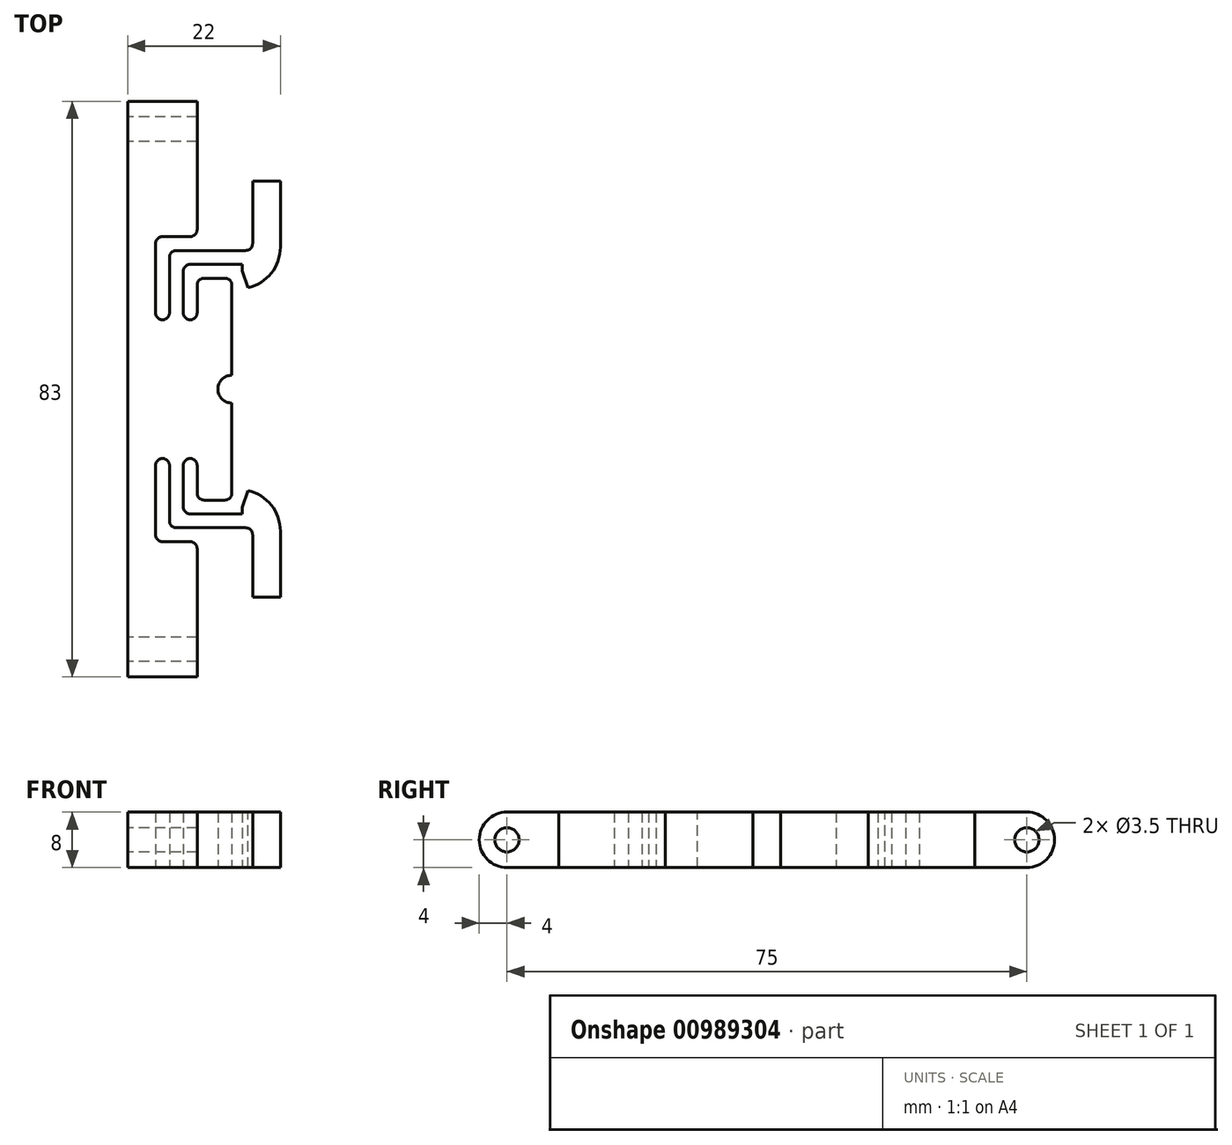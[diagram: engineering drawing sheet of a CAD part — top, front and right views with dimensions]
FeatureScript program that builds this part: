
annotation { "Feature Type Name" : "Feature", "Feature Type Description" : "" }
export const myFeature = defineFeature(function(context is Context, id is Id, definition is map)
    precondition{}
    {
        {
            var Q0;
            Q0=qCreatedBy(makeId("Top.planeOp"),FACE);
            var sketch = newSketch(context, id + "F0", { "sketchPlane" : qUnion([Q0])});
            skLineSegment(sketch, "E0.bottom", {"start": v(0, 0) * mm, "end": v(22, 0) * mm});
            skLineSegment(sketch, "E0.top", {"start": v(0, 83) * mm, "end": v(22, 83) * mm});
            skLineSegment(sketch, "E0.left", {"start": v(0, 0) * mm, "end": v(0, 83) * mm});
            skLineSegment(sketch, "E0.right", {"start": v(22, 0) * mm, "end": v(22, 83) * mm});
            skLineSegment(sketch, "E1", {"start": v(0, 41.5) * mm, "end": v(22, 41.5) * mm, "construction": true});
            skLineSegment(sketch, "E2.bottom", {"start": v(22, 59.5) * mm, "end": v(15, 59.5) * mm});
            skLineSegment(sketch, "E2.top", {"start": v(22, 23.5) * mm, "end": v(15, 23.5) * mm});
            skLineSegment(sketch, "E2.left", {"start": v(22, 59.5) * mm, "end": v(22, 23.5) * mm});
            skLineSegment(sketch, "E2.right", {"start": v(15, 59.5) * mm, "end": v(15, 23.5) * mm});
            skLineSegment(sketch, "E3", {"start": v(16.5, 59.5) * mm, "end": v(16.5, 23.5) * mm, "construction": true});
            skLineSegment(sketch, "E4.bottom", {"start": v(16.5, 59.5) * mm, "end": v(22, 59.5) * mm});
            skLineSegment(sketch, "E4.top", {"start": v(16.5, 56) * mm, "end": v(22, 56) * mm});
            skLineSegment(sketch, "E4.left", {"start": v(16.5, 59.5) * mm, "end": v(16.5, 56) * mm});
            skLineSegment(sketch, "E4.right", {"start": v(22, 59.5) * mm, "end": v(22, 56) * mm});
            skLineSegment(sketch, "E5.bottom", {"start": v(16.5, 23.5) * mm, "end": v(22, 23.5) * mm});
            skLineSegment(sketch, "E5.top", {"start": v(16.5, 27) * mm, "end": v(22, 27) * mm});
            skLineSegment(sketch, "E5.left", {"start": v(16.5, 23.5) * mm, "end": v(16.5, 27) * mm});
            skLineSegment(sketch, "E5.right", {"start": v(22, 23.5) * mm, "end": v(22, 27) * mm});
            skLineSegment(sketch, "E6", {"start": v(8, 83) * mm, "end": v(8, 0) * mm, "construction": true});
            skLineSegment(sketch, "E7.bottom", {"start": v(8, 63.5) * mm, "end": v(22, 63.5) * mm});
            skLineSegment(sketch, "E7.top", {"start": v(8, 61.5) * mm, "end": v(22, 61.5) * mm});
            skLineSegment(sketch, "E7.left", {"start": v(8, 63.5) * mm, "end": v(8, 61.5) * mm});
            skLineSegment(sketch, "E7.right", {"start": v(22, 63.5) * mm, "end": v(22, 61.5) * mm});
            skLineSegment(sketch, "E8.bottom", {"start": v(8, 21.5) * mm, "end": v(22, 21.5) * mm});
            skLineSegment(sketch, "E8.top", {"start": v(8, 19.5) * mm, "end": v(22, 19.5) * mm});
            skLineSegment(sketch, "E8.left", {"start": v(8, 21.5) * mm, "end": v(8, 19.5) * mm});
            skLineSegment(sketch, "E8.right", {"start": v(22, 21.5) * mm, "end": v(22, 19.5) * mm});
            skLineSegment(sketch, "E9.bottom", {"start": v(18, 61.5) * mm, "end": v(22, 61.5) * mm});
            skLineSegment(sketch, "E9.top", {"start": v(18, 71.5) * mm, "end": v(22, 71.5) * mm});
            skLineSegment(sketch, "E9.left", {"start": v(18, 61.5) * mm, "end": v(18, 71.5) * mm});
            skLineSegment(sketch, "E9.right", {"start": v(22, 61.5) * mm, "end": v(22, 71.5) * mm});
            skLineSegment(sketch, "E10.bottom", {"start": v(18, 21.5) * mm, "end": v(22, 21.5) * mm});
            skLineSegment(sketch, "E10.top", {"start": v(18, 11.5) * mm, "end": v(22, 11.5) * mm});
            skLineSegment(sketch, "E10.left", {"start": v(18, 21.5) * mm, "end": v(18, 11.5) * mm});
            skLineSegment(sketch, "E10.right", {"start": v(22, 21.5) * mm, "end": v(22, 11.5) * mm});
            skLineSegment(sketch, "E11.bottom", {"start": v(10, 63.5) * mm, "end": v(22, 63.5) * mm});
            skLineSegment(sketch, "E11.top", {"start": v(10, 73) * mm, "end": v(22, 73) * mm});
            skLineSegment(sketch, "E11.left", {"start": v(10, 63.5) * mm, "end": v(10, 73) * mm});
            skLineSegment(sketch, "E11.right", {"start": v(22, 63.5) * mm, "end": v(22, 73) * mm});
            skLineSegment(sketch, "E12.bottom", {"start": v(10, 19.5) * mm, "end": v(22, 19.5) * mm});
            skLineSegment(sketch, "E12.top", {"start": v(10, 10) * mm, "end": v(22, 10) * mm});
            skLineSegment(sketch, "E12.left", {"start": v(10, 19.5) * mm, "end": v(10, 10) * mm});
            skLineSegment(sketch, "E12.right", {"start": v(22, 19.5) * mm, "end": v(22, 10) * mm});
            skLineSegment(sketch, "E13.bottom", {"start": v(15, 59.5) * mm, "end": v(8, 59.5) * mm});
            skLineSegment(sketch, "E13.top", {"start": v(15, 57.5) * mm, "end": v(8, 57.5) * mm});
            skLineSegment(sketch, "E13.left", {"start": v(15, 59.5) * mm, "end": v(15, 57.5) * mm});
            skLineSegment(sketch, "E13.right", {"start": v(8, 59.5) * mm, "end": v(8, 57.5) * mm});
            skLineSegment(sketch, "E14.bottom", {"start": v(15, 23.5) * mm, "end": v(8, 23.5) * mm});
            skLineSegment(sketch, "E14.top", {"start": v(15, 25.5) * mm, "end": v(8, 25.5) * mm});
            skLineSegment(sketch, "E14.left", {"start": v(15, 23.5) * mm, "end": v(15, 25.5) * mm});
            skLineSegment(sketch, "E14.right", {"start": v(8, 23.5) * mm, "end": v(8, 25.5) * mm});
            skLineSegment(sketch, "E15.bottom", {"start": v(8, 57.5) * mm, "end": v(10, 57.5) * mm});
            skLineSegment(sketch, "E15.top", {"start": v(8, 51.5) * mm, "end": v(10, 51.5) * mm});
            skLineSegment(sketch, "E15.left", {"start": v(8, 57.5) * mm, "end": v(8, 51.5) * mm});
            skLineSegment(sketch, "E15.right", {"start": v(10, 57.5) * mm, "end": v(10, 51.5) * mm});
            skLineSegment(sketch, "E16.bottom", {"start": v(8, 25.5) * mm, "end": v(10, 25.5) * mm});
            skLineSegment(sketch, "E16.top", {"start": v(8, 31.5) * mm, "end": v(10, 31.5) * mm});
            skLineSegment(sketch, "E16.left", {"start": v(8, 25.5) * mm, "end": v(8, 31.5) * mm});
            skLineSegment(sketch, "E16.right", {"start": v(10, 25.5) * mm, "end": v(10, 31.5) * mm});
            skLineSegment(sketch, "E17.bottom", {"start": v(6, 21.5) * mm, "end": v(8, 21.5) * mm});
            skLineSegment(sketch, "E17.top", {"start": v(6, 31.5) * mm, "end": v(8, 31.5) * mm});
            skLineSegment(sketch, "E17.left", {"start": v(6, 21.5) * mm, "end": v(6, 31.5) * mm});
            skLineSegment(sketch, "E17.right", {"start": v(8, 21.5) * mm, "end": v(8, 31.5) * mm});
            skPoint(sketch, "E18.oppositeSnap0", {"position": v(6, 26.5) * mm});
            skLineSegment(sketch, "E18.bottom", {"start": v(8, 51.5) * mm, "end": v(6, 51.5) * mm});
            skLineSegment(sketch, "E18.top", {"start": v(8, 61.5) * mm, "end": v(6, 61.5) * mm});
            skLineSegment(sketch, "E18.left", {"start": v(8, 51.5) * mm, "end": v(8, 61.5) * mm});
            skLineSegment(sketch, "E18.right", {"start": v(6, 51.5) * mm, "end": v(6, 61.5) * mm});
            skLineSegment(sketch, "E19.bottom", {"start": v(8, 19.5) * mm, "end": v(4, 19.5) * mm});
            skLineSegment(sketch, "E19.top", {"start": v(8, 31.5) * mm, "end": v(4, 31.5) * mm});
            skLineSegment(sketch, "E19.left", {"start": v(8, 19.5) * mm, "end": v(8, 31.5) * mm});
            skLineSegment(sketch, "E19.right", {"start": v(4, 19.5) * mm, "end": v(4, 31.5) * mm});
            skLineSegment(sketch, "E20.bottom", {"start": v(8, 63.5) * mm, "end": v(4, 63.5) * mm});
            skLineSegment(sketch, "E20.top", {"start": v(8, 51.5) * mm, "end": v(4, 51.5) * mm});
            skLineSegment(sketch, "E20.left", {"start": v(8, 63.5) * mm, "end": v(8, 51.5) * mm});
            skLineSegment(sketch, "E20.right", {"start": v(4, 63.5) * mm, "end": v(4, 51.5) * mm});
            skLineSegment(sketch, "E21.top", {"start": v(10, 0) * mm, "end": v(22, 0) * mm});
            skLineSegment(sketch, "E21.left", {"start": v(10, 10) * mm, "end": v(10, 0) * mm});
            skLineSegment(sketch, "E21.right", {"start": v(22, 10) * mm, "end": v(22, 0) * mm});
            skLineSegment(sketch, "E22.top", {"start": v(10, 83) * mm, "end": v(22, 83) * mm});
            skLineSegment(sketch, "E22.left", {"start": v(10, 73) * mm, "end": v(10, 83) * mm});
            skLineSegment(sketch, "E22.right", {"start": v(22, 73) * mm, "end": v(22, 83) * mm});
            skSolve(sketch);
        }
        {
            var Q0;
            {var subQ12=sQuery(id+"F0.wireOp",EDGE,"E0.left");Q0=makeQuery(id+"F0.imprint","IMPRINT",FACE,{"disambiguationData":[TD([[makeQuery(id+"F0.imprint","IMPRINT",EDGE,{"derivedFrom":subQ12}),-1.0]])]});}
            var Q1;
            {var subQ0=sQuery(id+"F0.wireOp",EDGE,"E9.top");Q1=makeQuery(id+"F0.imprint","IMPRINT",FACE,{"disambiguationData":[TD([[makeQuery(id+"F0.imprint","IMPRINT",EDGE,{"derivedFrom":subQ0}),-1.0]])]});}
            var Q2;
            {var subQ0=sQuery(id+"F0.wireOp",EDGE,"E7.top");var subQ1=sQuery(id+"F0.wireOp",EDGE,"E0.right");var subQ2=makeQuery(id+"F0.imprint","INTERSECT",VERTEX,{"derivedFrom":[subQ1,subQ0]});Q2=makeQuery(id+"F0.imprint","IMPRINT",FACE,{"disambiguationData":[TD([[makeQuery(id+"F0.imprint","IMPRINT",EDGE,{"disambiguationData":[TD([[subQ2,-1.0]])],"derivedFrom":subQ1}),1.0]])]});}
            var Q3;
            {var subQ3=sQuery(id+"F0.wireOp",EDGE,"E4.top");Q3=makeQuery(id+"F0.imprint","IMPRINT",FACE,{"disambiguationData":[TD([[makeQuery(id+"F0.imprint","IMPRINT",EDGE,{"derivedFrom":subQ3}),1.0]])]});}
            var Q4;
            {var subQ0=sQuery(id+"F0.wireOp",EDGE,"E5.top");Q4=makeQuery(id+"F0.imprint","IMPRINT",FACE,{"disambiguationData":[TD([[makeQuery(id+"F0.imprint","IMPRINT",EDGE,{"derivedFrom":subQ0}),-1.0]])]});}
            var Q5;
            {var subQ0=sQuery(id+"F0.wireOp",EDGE,"E8.bottom");var subQ1=sQuery(id+"F0.wireOp",EDGE,"E0.right");var subQ2=makeQuery(id+"F0.imprint","INTERSECT",VERTEX,{"derivedFrom":[subQ1,subQ0]});Q5=makeQuery(id+"F0.imprint","IMPRINT",FACE,{"disambiguationData":[TD([[makeQuery(id+"F0.imprint","IMPRINT",EDGE,{"disambiguationData":[TD([[subQ2,1.0]])],"derivedFrom":subQ1}),1.0]])]});}
            var Q6;
            {var subQ0=sQuery(id+"F0.wireOp",EDGE,"E10.top");Q6=makeQuery(id+"F0.imprint","IMPRINT",FACE,{"disambiguationData":[TD([[makeQuery(id+"F0.imprint","IMPRINT",EDGE,{"derivedFrom":subQ0}),1.0]])]});}
            var Q7;
            {var subQ0=sQuery(id+"F0.wireOp",EDGE,"E14.bottom");Q7=makeQuery(id+"F0.imprint","IMPRINT",FACE,{"disambiguationData":[TD([[makeQuery(id+"F0.imprint","IMPRINT",EDGE,{"derivedFrom":subQ0}),1.0]])]});}
            var Q8;
            Q8=makeQuery(id+"F0.imprint","IMPRINT",FACE,{"disambiguationData":[TD([[makeQuery(id+"F0.imprint","IMPRINT",EDGE,{"derivedFrom":sQuery(id+"F0.wireOp",EDGE,"E14.right")}),1.0]])]});
            var Q9;
            Q9=makeQuery(id+"F0.imprint","IMPRINT",FACE,{"disambiguationData":[TD([[makeQuery(id+"F0.imprint","IMPRINT",EDGE,{"derivedFrom":sQuery(id+"F0.wireOp",EDGE,"E13.right")}),-1.0]])]});
            var Q10;
            {var subQ3=sQuery(id+"F0.wireOp",EDGE,"E13.bottom");Q10=makeQuery(id+"F0.imprint","IMPRINT",FACE,{"disambiguationData":[TD([[makeQuery(id+"F0.imprint","IMPRINT",EDGE,{"derivedFrom":subQ3}),-1.0]])]});}
            extrude(context, id + "F1", {"entities" : qUnion([Q0, Q1, Q2, Q3, Q4, Q5, Q6, Q7, Q8, Q9, Q10]), "depth" : 8 * mm, "offsetDistance" : 25 * mm});
        }
        {
            var Q0;
            Q0=makeQuery(id+"F1.opExtrude","CAP_EDGE",EDGE,{"disambiguationData":[OSD([sQuery(id+"F0.wireOp",EDGE,"E0.top")])],"isStart":false});
            var Q1;
            Q1=makeQuery(id+"F1.opExtrude","CAP_EDGE",EDGE,{"disambiguationData":[OSD([sQuery(id+"F0.wireOp",EDGE,"E0.bottom")])],"isStart":false});
            var Q2;
            Q2=makeQuery(id+"F1.opExtrude","CAP_EDGE",EDGE,{"disambiguationData":[OSD([sQuery(id+"F0.wireOp",EDGE,"E0.bottom")])],"isStart":true});
            var Q3;
            Q3=makeQuery(id+"F1.opExtrude","CAP_EDGE",EDGE,{"disambiguationData":[OSD([sQuery(id+"F0.wireOp",EDGE,"E0.top")])],"isStart":true});
            fillet(context, id + "F2", {"entities" : qUnion([Q0, Q1, Q2, Q3]), "radius" : 4 * mm, "tangentPropagation" : true, "allowEdgeOverflow" : false});
        }
        {
            var Q0;
            Q0=makeQuery(id+"F1.opExtrude","SWEPT_EDGE",EDGE,{"disambiguationData":[OSD([sQuery(id+"F0.wireOp",EDGE,"E0.right"),sQuery(id+"F0.wireOp",EDGE,"E4.top")])]});
            var Q1;
            Q1=makeQuery(id+"F1.opExtrude","SWEPT_EDGE",EDGE,{"disambiguationData":[OSD([sQuery(id+"F0.wireOp",EDGE,"E0.right"),sQuery(id+"F0.wireOp",EDGE,"E5.top")])]});
            fillet(context, id + "F3", {"entities" : qUnion([Q0, Q1]), "radius" : 6 * mm, "tangentPropagation" : true, "allowEdgeOverflow" : false});
        }
        {
            var Q0;
            Q0=makeQuery(id+"F3.opFillet","BLEND_EDGE",EDGE,{"blendedFrom":[makeQuery(id+"F1.opExtrude","SWEPT_EDGE",EDGE,{"disambiguationData":[OSD([sQuery(id+"F0.wireOp",EDGE,"E0.right"),sQuery(id+"F0.wireOp",EDGE,"E4.top")])]}),makeQuery(id+"F1.opExtrude","SWEPT_FACE",FACE,{"disambiguationData":[OSD([sQuery(id+"F0.wireOp",EDGE,"E4.left")])]})],"blendedInto":[makeQuery(id+"F1.opExtrude","SWEPT_FACE",FACE,{"disambiguationData":[OSD([sQuery(id+"F0.wireOp",EDGE,"E4.left")])]})]});
            chamfer(context, id + "F4", {"entities" : qUnion([Q0]), "chamferType" : ChamferType.TWO_OFFSETS, "width1" : 0.5 * mm, "oppositeDirection" : false, "width2" : 2.5 * mm, "tangentPropagation" : true});
        }
        {
            var Q0;
            Q0=makeQuery(id+"F3.opFillet","BLEND_EDGE",EDGE,{"blendedFrom":[makeQuery(id+"F1.opExtrude","SWEPT_EDGE",EDGE,{"disambiguationData":[OSD([sQuery(id+"F0.wireOp",EDGE,"E0.right"),sQuery(id+"F0.wireOp",EDGE,"E5.top")])]}),makeQuery(id+"F1.opExtrude","SWEPT_FACE",FACE,{"disambiguationData":[OSD([sQuery(id+"F0.wireOp",EDGE,"E5.left")])]})],"blendedInto":[makeQuery(id+"F1.opExtrude","SWEPT_FACE",FACE,{"disambiguationData":[OSD([sQuery(id+"F0.wireOp",EDGE,"E5.left")])]})]});
            chamfer(context, id + "F5", {"entities" : qUnion([Q0]), "chamferType" : ChamferType.TWO_OFFSETS, "width1" : 0.5 * mm, "oppositeDirection" : true, "width2" : 2.5 * mm, "tangentPropagation" : true});
        }
        {
            var Q0;
            Q0=makeQuery(id+"F1.opExtrude","CAP_FACE",FACE,{"disambiguationData":[OSD([sQuery(id+"F0.wireOp",EDGE,"E0.bottom"),sQuery(id+"F0.wireOp",EDGE,"E0.top"),sQuery(id+"F0.wireOp",EDGE,"E0.left"),sQuery(id+"F0.wireOp",EDGE,"E0.right"),sQuery(id+"F0.wireOp",EDGE,"E2.bottom"),sQuery(id+"F0.wireOp",EDGE,"E2.top"),sQuery(id+"F0.wireOp",EDGE,"E2.right"),sQuery(id+"F0.wireOp",EDGE,"E4.top"),sQuery(id+"F0.wireOp",EDGE,"E4.left"),sQuery(id+"F0.wireOp",EDGE,"E5.top"),sQuery(id+"F0.wireOp",EDGE,"E5.left"),sQuery(id+"F0.wireOp",EDGE,"E7.bottom"),sQuery(id+"F0.wireOp",EDGE,"E7.top"),sQuery(id+"F0.wireOp",EDGE,"E8.bottom"),sQuery(id+"F0.wireOp",EDGE,"E8.top"),sQuery(id+"F0.wireOp",EDGE,"E9.top"),sQuery(id+"F0.wireOp",EDGE,"E9.left"),sQuery(id+"F0.wireOp",EDGE,"E10.top"),sQuery(id+"F0.wireOp",EDGE,"E10.left"),sQuery(id+"F0.wireOp",EDGE,"E11.left"),sQuery(id+"F0.wireOp",EDGE,"E12.left"),sQuery(id+"F0.wireOp",EDGE,"E13.bottom"),sQuery(id+"F0.wireOp",EDGE,"E13.top"),sQuery(id+"F0.wireOp",EDGE,"E13.right"),sQuery(id+"F0.wireOp",EDGE,"E14.bottom"),sQuery(id+"F0.wireOp",EDGE,"E14.top"),sQuery(id+"F0.wireOp",EDGE,"E14.right"),sQuery(id+"F0.wireOp",EDGE,"E15.top"),sQuery(id+"F0.wireOp",EDGE,"E15.left"),sQuery(id+"F0.wireOp",EDGE,"E15.right"),sQuery(id+"F0.wireOp",EDGE,"E16.top"),sQuery(id+"F0.wireOp",EDGE,"E16.left"),sQuery(id+"F0.wireOp",EDGE,"E16.right"),sQuery(id+"F0.wireOp",EDGE,"E17.bottom"),sQuery(id+"F0.wireOp",EDGE,"E17.left"),sQuery(id+"F0.wireOp",EDGE,"E18.top"),sQuery(id+"F0.wireOp",EDGE,"E18.right"),sQuery(id+"F0.wireOp",EDGE,"E19.bottom"),sQuery(id+"F0.wireOp",EDGE,"E19.top"),sQuery(id+"F0.wireOp",EDGE,"E19.right"),sQuery(id+"F0.wireOp",EDGE,"E20.bottom"),sQuery(id+"F0.wireOp",EDGE,"E20.top"),sQuery(id+"F0.wireOp",EDGE,"E20.right"),sQuery(id+"F0.wireOp",EDGE,"E21.left"),sQuery(id+"F0.wireOp",EDGE,"E22.left")])],"isStart":true});
            var sketch = newSketch(context, id + "F6", { "sketchPlane" : qUnion([Q0])});
            skCircle(sketch, "E23", {"center": v(15, -41.5) * mm, "radius": 2 * mm});
            skSolve(sketch);
        }
        {
            var Q0;
            {var subQ0=sQuery(id+"F6.wireOp",EDGE,"E23");var subQ1=makeQuery(id+"F1.opExtrude","CAP_EDGE",EDGE,{"disambiguationData":[OSD([sQuery(id+"F0.wireOp",EDGE,"E2.right")])],"isStart":true});var subQ2=makeQuery(id+"F6.imprint","INTERSECT",VERTEX,{"disambiguationData":[OD(0.0)],"derivedFrom":[subQ1,subQ0]});Q0=makeQuery(id+"F6.imprint","IMPRINT",FACE,{"disambiguationData":[TD([[makeQuery(id+"F6.imprint","IMPRINT",EDGE,{"disambiguationData":[TD([[subQ2,1.0]])],"derivedFrom":subQ0}),1.0]])]});}
            extrude(context, id + "F7", {"entities" : qUnion([Q0]), "operationType" : NewBodyOperationType.REMOVE, "oppositeDirection" : true, "depth" : 8 * mm, "offsetDistance" : 25 * mm});
        }
        {
            var Q0;
            Q0=makeQuery(id+"F1.opExtrude","SWEPT_EDGE",EDGE,{"disambiguationData":[OSD([sQuery(id+"F0.wireOp",EDGE,"E8.bottom"),sQuery(id+"F0.wireOp",EDGE,"E10.left")])]});
            var Q1;
            Q1=makeQuery(id+"F1.opExtrude","SWEPT_EDGE",EDGE,{"disambiguationData":[OSD([sQuery(id+"F0.wireOp",EDGE,"E17.bottom"),sQuery(id+"F0.wireOp",EDGE,"E17.left")])]});
            var Q2;
            Q2=makeQuery(id+"F1.opExtrude","SWEPT_EDGE",EDGE,{"disambiguationData":[OSD([sQuery(id+"F0.wireOp",EDGE,"E19.bottom"),sQuery(id+"F0.wireOp",EDGE,"E19.right")])]});
            var Q3;
            Q3=makeQuery(id+"F1.opExtrude","SWEPT_EDGE",EDGE,{"disambiguationData":[OSD([sQuery(id+"F0.wireOp",EDGE,"E8.top"),sQuery(id+"F0.wireOp",EDGE,"E12.left")])]});
            var Q4;
            Q4=makeQuery(id+"F1.opExtrude","SWEPT_EDGE",EDGE,{"disambiguationData":[OSD([sQuery(id+"F0.wireOp",EDGE,"E14.bottom"),sQuery(id+"F0.wireOp",EDGE,"E14.right"),sQuery(id+"F0.wireOp",EDGE,"E17.right")])]});
            var Q5;
            Q5=makeQuery(id+"F1.opExtrude","SWEPT_EDGE",EDGE,{"disambiguationData":[OSD([sQuery(id+"F0.wireOp",EDGE,"E2.right"),sQuery(id+"F0.wireOp",EDGE,"E14.top")])]});
            var Q6;
            Q6=makeQuery(id+"F1.opExtrude","SWEPT_EDGE",EDGE,{"disambiguationData":[OSD([sQuery(id+"F0.wireOp",EDGE,"E14.top"),sQuery(id+"F0.wireOp",EDGE,"E16.right")])]});
            var Q7;
            Q7=makeQuery(id+"F1.opExtrude","SWEPT_EDGE",EDGE,{"disambiguationData":[OSD([sQuery(id+"F0.wireOp",EDGE,"E16.top"),sQuery(id+"F0.wireOp",EDGE,"E16.left"),sQuery(id+"F0.wireOp",EDGE,"E17.top")])]});
            var Q8;
            Q8=makeQuery(id+"F1.opExtrude","SWEPT_EDGE",EDGE,{"disambiguationData":[OSD([sQuery(id+"F0.wireOp",EDGE,"E16.top"),sQuery(id+"F0.wireOp",EDGE,"E16.right")])]});
            var Q9;
            Q9=makeQuery(id+"F1.opExtrude","SWEPT_EDGE",EDGE,{"disambiguationData":[OSD([sQuery(id+"F0.wireOp",EDGE,"E17.top"),sQuery(id+"F0.wireOp",EDGE,"E17.left"),sQuery(id+"F0.wireOp",EDGE,"E19.top")])]});
            var Q10;
            Q10=makeQuery(id+"F1.opExtrude","SWEPT_EDGE",EDGE,{"disambiguationData":[OSD([sQuery(id+"F0.wireOp",EDGE,"E19.top"),sQuery(id+"F0.wireOp",EDGE,"E19.right")])]});
            var Q11;
            Q11=makeQuery(id+"F1.opExtrude","SWEPT_EDGE",EDGE,{"disambiguationData":[OSD([sQuery(id+"F0.wireOp",EDGE,"E18.bottom"),sQuery(id+"F0.wireOp",EDGE,"E18.right"),sQuery(id+"F0.wireOp",EDGE,"E20.top")])]});
            var Q12;
            Q12=makeQuery(id+"F1.opExtrude","SWEPT_EDGE",EDGE,{"disambiguationData":[OSD([sQuery(id+"F0.wireOp",EDGE,"E15.top"),sQuery(id+"F0.wireOp",EDGE,"E15.right")])]});
            var Q13;
            Q13=makeQuery(id+"F1.opExtrude","SWEPT_EDGE",EDGE,{"disambiguationData":[OSD([sQuery(id+"F0.wireOp",EDGE,"E7.top"),sQuery(id+"F0.wireOp",EDGE,"E9.left")])]});
            var Q14;
            Q14=makeQuery(id+"F1.opExtrude","SWEPT_EDGE",EDGE,{"disambiguationData":[OSD([sQuery(id+"F0.wireOp",EDGE,"E18.top"),sQuery(id+"F0.wireOp",EDGE,"E18.right")])]});
            var Q15;
            Q15=makeQuery(id+"F1.opExtrude","SWEPT_EDGE",EDGE,{"disambiguationData":[OSD([sQuery(id+"F0.wireOp",EDGE,"E13.top"),sQuery(id+"F0.wireOp",EDGE,"E15.right")])]});
            var Q16;
            Q16=makeQuery(id+"F1.opExtrude","SWEPT_EDGE",EDGE,{"disambiguationData":[OSD([sQuery(id+"F0.wireOp",EDGE,"E2.right"),sQuery(id+"F0.wireOp",EDGE,"E13.top")])]});
            var Q17;
            Q17=makeQuery(id+"F1.opExtrude","SWEPT_EDGE",EDGE,{"disambiguationData":[OSD([sQuery(id+"F0.wireOp",EDGE,"E13.bottom"),sQuery(id+"F0.wireOp",EDGE,"E13.right"),sQuery(id+"F0.wireOp",EDGE,"E18.left")])]});
            var Q18;
            Q18=makeQuery(id+"F1.opExtrude","SWEPT_EDGE",EDGE,{"disambiguationData":[OSD([sQuery(id+"F0.wireOp",EDGE,"E20.top"),sQuery(id+"F0.wireOp",EDGE,"E20.right")])]});
            var Q19;
            Q19=makeQuery(id+"F1.opExtrude","SWEPT_EDGE",EDGE,{"disambiguationData":[OSD([sQuery(id+"F0.wireOp",EDGE,"E15.top"),sQuery(id+"F0.wireOp",EDGE,"E15.left"),sQuery(id+"F0.wireOp",EDGE,"E18.bottom")])]});
            var Q20;
            Q20=makeQuery(id+"F1.opExtrude","SWEPT_EDGE",EDGE,{"disambiguationData":[OSD([sQuery(id+"F0.wireOp",EDGE,"E20.bottom"),sQuery(id+"F0.wireOp",EDGE,"E20.right")])]});
            var Q21;
            Q21=makeQuery(id+"F1.opExtrude","SWEPT_EDGE",EDGE,{"disambiguationData":[OSD([sQuery(id+"F0.wireOp",EDGE,"E7.bottom"),sQuery(id+"F0.wireOp",EDGE,"E11.left")])]});
            fillet(context, id + "F8", {"entities" : qUnion([Q0, Q1, Q2, Q3, Q4, Q5, Q6, Q7, Q8, Q9, Q10, Q11, Q12, Q13, Q14, Q15, Q16, Q17, Q18, Q19, Q20, Q21]), "radius" : 1 * mm, "tangentPropagation" : true, "allowEdgeOverflow" : false});
        }
        {
            var Q0;
            Q0=makeQuery(id+"F1.opExtrude","SWEPT_FACE",FACE,{"disambiguationData":[OSD([sQuery(id+"F0.wireOp",EDGE,"E0.left")])]});
            var sketch = newSketch(context, id + "F9", { "sketchPlane" : qUnion([Q0])});
            skLineSegment(sketch, "E24", {"start": v(-83, 4) * mm, "end": v(0, 4) * mm, "construction": true});
            skCircle(sketch, "E25", {"center": v(-79, 4) * mm, "radius": 1.75 * mm});
            skCircle(sketch, "E26", {"center": v(-4, 4) * mm, "radius": 1.75 * mm});
            skSolve(sketch);
        }
        {
            var Q0;
            Q0 = qSketchRegion(id + "F9", true);
            extrude(context, id + "F10", {"entities" : qUnion([Q0]), "operationType" : NewBodyOperationType.REMOVE, "oppositeDirection" : true, "depth" : 10 * mm, "offsetDistance" : 25 * mm});
        }
    });
